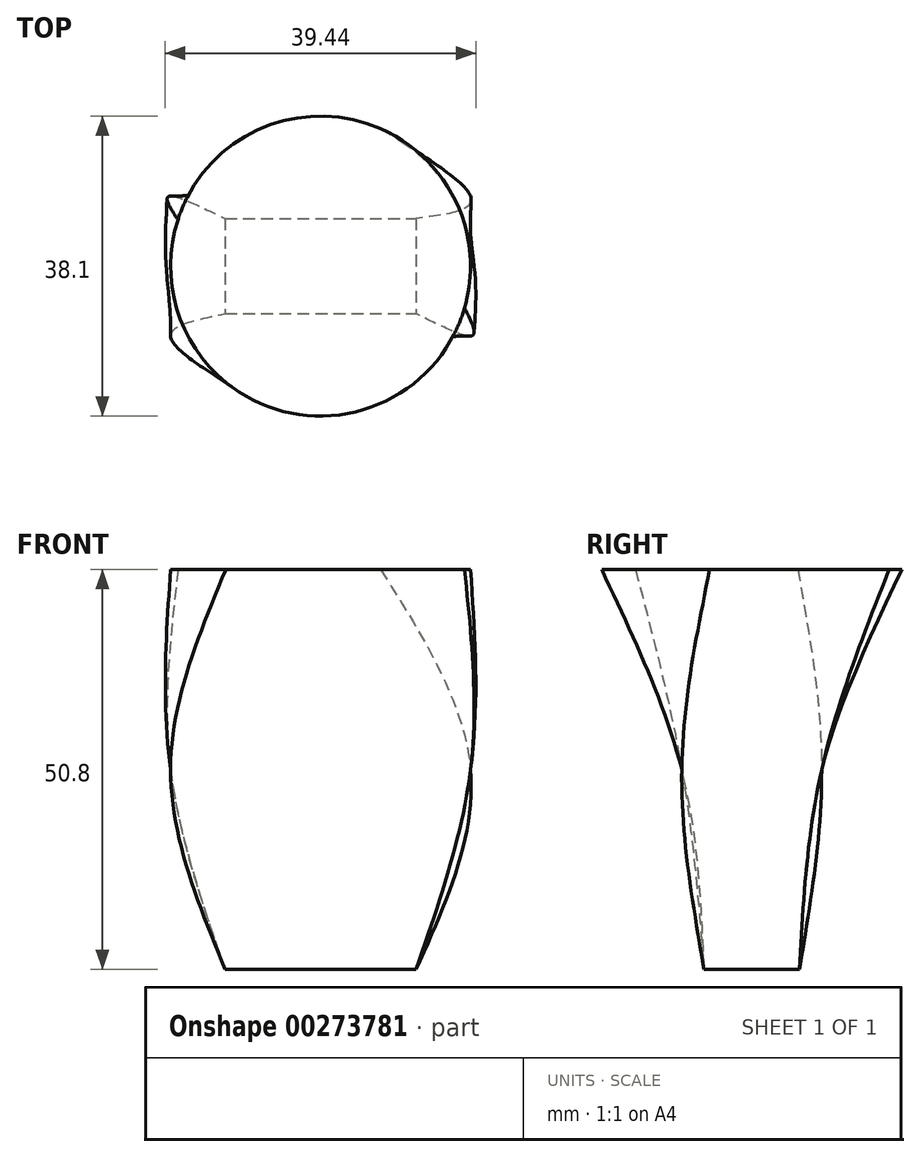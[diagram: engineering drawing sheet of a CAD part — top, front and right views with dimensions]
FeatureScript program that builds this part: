
annotation { "Feature Type Name" : "Feature", "Feature Type Description" : "" }
export const myFeature = defineFeature(function(context is Context, id is Id, definition is map)
    precondition{}
    {
        {
            var Q0;
            Q0=qCreatedBy(makeId("Top.planeOp"),FACE);
            var sketch = newSketch(context, id + "F0", { "sketchPlane" : qUnion([Q0])});
            skArc(sketch, "E0", {"start": v(-12.03, -14.77) * mm, "mid": v(5.66, -18.19) * mm, "end": v(18.29, -5.34) * mm});
            skArc(sketch, "E1", {"start": v(-18.12, 5.87) * mm, "mid": v(-18.27, -5.4) * mm, "end": v(-12.03, -14.77) * mm});
            skArc(sketch, "E2", {"start": v(7.63, 17.45) * mm, "mid": v(-7.81, 17.37) * mm, "end": v(-18.12, 5.87) * mm});
            skArc(sketch, "E3", {"start": v(18.29, -5.34) * mm, "mid": v(17.26, 8.07) * mm, "end": v(7.63, 17.45) * mm});
            skSolve(sketch);
        }
        {
            var Q0;
            Q0=qCreatedBy(makeId("Top.planeOp"),FACE);
            cPlane(context, id + "F1", {"entities" : qUnion([Q0]), "cplaneType" : CPlaneType.OFFSET, "offset" : 25.4 * mm, "oppositeDirection" : true, "width" : 152.4 * mm, "height" : 152.4 * mm});
        }
        {
            var Q0;
            Q0=qCreatedBy(id+"F1.planeOp",FACE);
            var sketch = newSketch(context, id + "F2", { "sketchPlane" : qUnion([Q0])});
            skLineSegment(sketch, "E4.bottom", {"start": v(-19.05, -8.9) * mm, "end": v(19.05, -8.9) * mm});
            skLineSegment(sketch, "E4.top", {"start": v(-19.05, 8.9) * mm, "end": v(19.05, 8.9) * mm});
            skLineSegment(sketch, "E4.left", {"start": v(-19.05, -8.9) * mm, "end": v(-19.05, 8.9) * mm});
            skLineSegment(sketch, "E4.right", {"start": v(19.05, -8.9) * mm, "end": v(19.05, 8.9) * mm});
            skPoint(sketch, "E4.middle", {"position": v(0, 0) * mm});
            skSolve(sketch);
        }
        {
            var Q0;
            Q0=qCreatedBy(id+"F1.planeOp",FACE);
            cPlane(context, id + "F3", {"entities" : qUnion([Q0]), "cplaneType" : CPlaneType.OFFSET, "offset" : 25.4 * mm, "oppositeDirection" : true, "width" : 152.4 * mm, "height" : 152.4 * mm});
        }
        {
            var Q0;
            Q0=qCreatedBy(id+"F3.planeOp",FACE);
            var sketch = newSketch(context, id + "F4", { "sketchPlane" : qUnion([Q0])});
            skLineSegment(sketch, "E5.bottom", {"start": v(-12.14, 6.05) * mm, "end": v(12.14, 6.05) * mm});
            skLineSegment(sketch, "E5.top", {"start": v(-12.14, -6.05) * mm, "end": v(12.14, -6.05) * mm});
            skLineSegment(sketch, "E5.left", {"start": v(-12.14, 6.05) * mm, "end": v(-12.14, -6.05) * mm});
            skLineSegment(sketch, "E5.right", {"start": v(12.14, 6.05) * mm, "end": v(12.14, -6.05) * mm});
            skPoint(sketch, "E5.middle", {"position": v(0, 0) * mm});
            skSolve(sketch);
        }
        {
            var Q0;
            Q0=makeQuery(id+"F0.imprint","IMPRINT",FACE,{"disambiguationData":[TD([[makeQuery(id+"F0.imprint","IMPRINT",EDGE,{"derivedFrom":sQuery(id+"F0.wireOp",EDGE,"E0")}),1.0]])]});
            var Q1;
            Q1=makeQuery(id+"F2.imprint","IMPRINT",FACE,{"disambiguationData":[TD([[makeQuery(id+"F2.imprint","IMPRINT",EDGE,{"derivedFrom":sQuery(id+"F2.wireOp",EDGE,"E4.bottom")}),1.0]])]});
            var Q2;
            Q2=makeQuery(id+"F4.imprint","IMPRINT",FACE,{"disambiguationData":[TD([[makeQuery(id+"F4.imprint","IMPRINT",EDGE,{"derivedFrom":sQuery(id+"F4.wireOp",EDGE,"E5.bottom")}),-1.0]])]});
            loft(context, id + "F5", {"sheetProfilesArray" : [{ "sheetProfileEntities" : qUnion([Q0]) }, { "sheetProfileEntities" : qUnion([Q1]) }, { "sheetProfileEntities" : qUnion([Q2]) }]});
        }
    });
